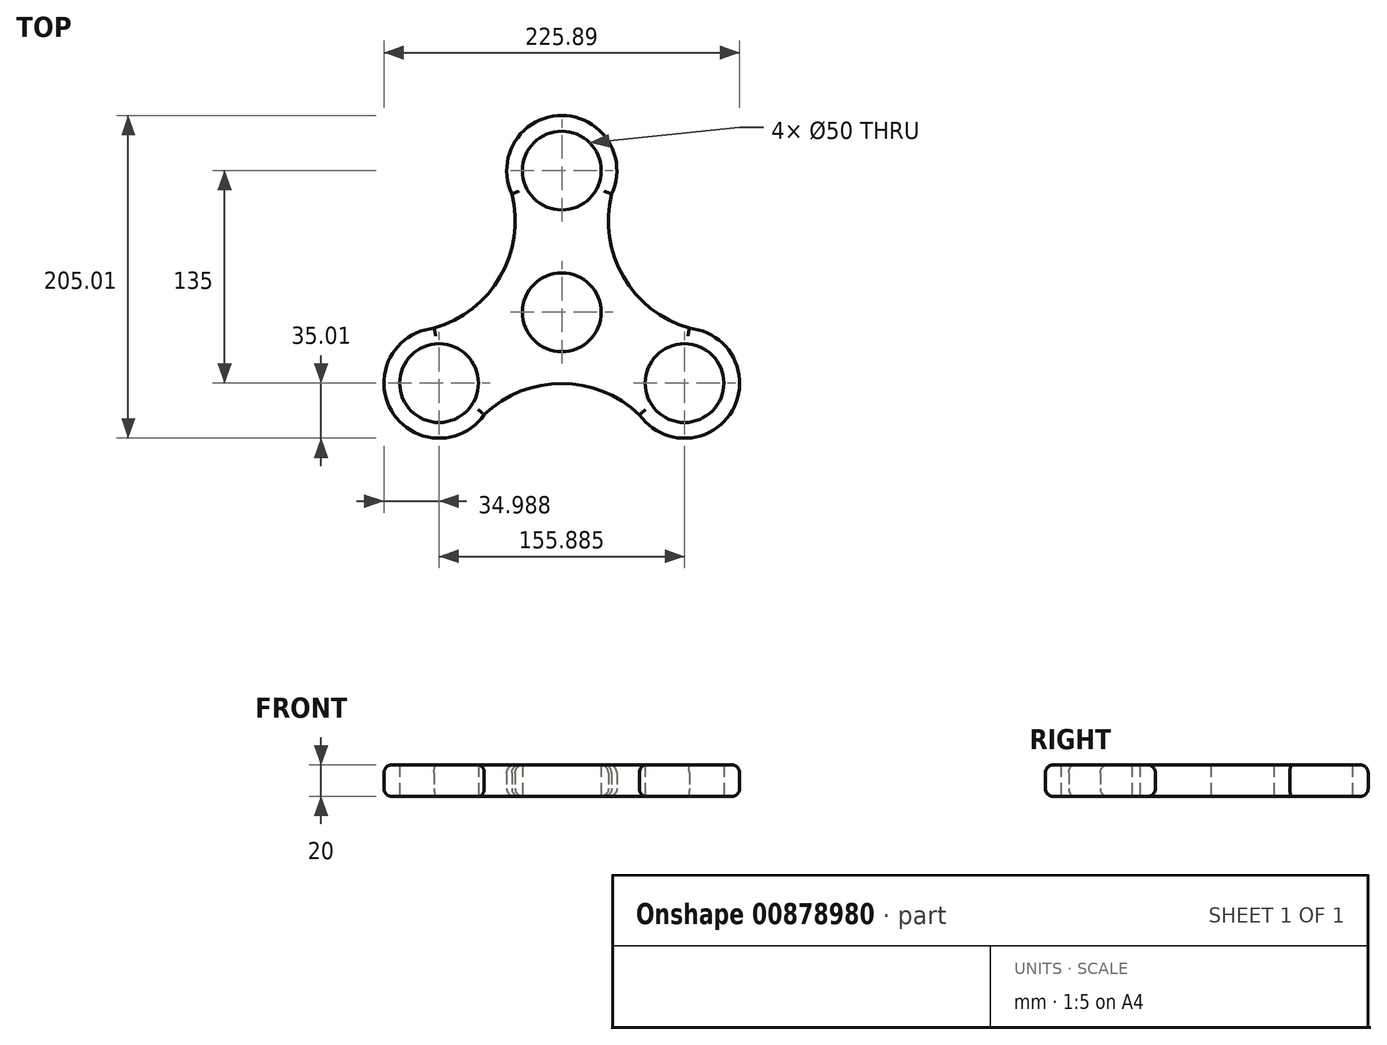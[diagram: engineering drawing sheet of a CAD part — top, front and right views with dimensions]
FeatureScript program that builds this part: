
annotation { "Feature Type Name" : "Feature", "Feature Type Description" : "" }
export const myFeature = defineFeature(function(context is Context, id is Id, definition is map)
    precondition{}
    {
        {
            var Q0;
            Q0=qCreatedBy(makeId("Top.planeOp"),FACE);
            var sketch = newSketch(context, id + "F0", { "sketchPlane" : qUnion([Q0])});
            skCircle(sketch, "E0", {"center": v(0, 0) * mm, "radius": 25 * mm});
            skCircle(sketch, "E1", {"center": v(0, 90) * mm, "radius": 25 * mm});
            skCircle(sketch, "E2.1.0", {"center": v(77.94, -45) * mm, "radius": 25 * mm});
            skCircle(sketch, "E2.2.0", {"center": v(-77.94, -45) * mm, "radius": 25 * mm});
            skLineSegment(sketch, "E2.anchor1", {"start": v(0, 0) * mm, "end": v(0, 90) * mm, "construction": true});
            skLineSegment(sketch, "E2.anchor2", {"start": v(0, 0) * mm, "end": v(-77.94, -45) * mm, "construction": true});
            skCircle(sketch, "E3", {"center": v(0, 90) * mm, "radius": 35 * mm});
            skCircle(sketch, "E4.1.0", {"center": v(-77.93, -45.01) * mm, "radius": 35 * mm});
            skCircle(sketch, "E4.2.0", {"center": v(77.96, -45) * mm, "radius": 35 * mm});
            skLineSegment(sketch, "E5", {"start": v(0, 90) * mm, "end": v(77.94, -45) * mm, "construction": true});
            skLineSegment(sketch, "E6", {"start": v(34.46, 83.85) * mm, "end": v(89.84, -12.07) * mm, "construction": true});
            skArc(sketch, "E7", {"start": v(34.46, 83.85) * mm, "mid": v(39.14, 22.6) * mm, "end": v(89.84, -12.07) * mm});
            skArc(sketch, "E8.1.0", {"start": v(-89.85, -12.09) * mm, "mid": v(-39.15, 22.6) * mm, "end": v(-34.46, 83.84) * mm});
            skArc(sketch, "E8.2.0", {"start": v(55.39, -71.77) * mm, "mid": v(0, -45.2) * mm, "end": v(-55.37, -71.77) * mm});
            skLineSegment(sketch, "E9.anchor1", {"start": v(0, 0) * mm, "end": v(0, 41.01) * mm, "construction": true});
            skLineSegment(sketch, "E9.anchor2", {"start": v(0, 0) * mm, "end": v(-31.42, 26.36) * mm, "construction": true});
            skPoint(sketch, "E10.0.midPoint", {"position": v(13.3, 35.84) * mm});
            skSolve(sketch);
        }
        {
            var Q0;
            Q0 = qSketchRegion(id + "F0", true);
            extrude(context, id + "F1", {"entities" : qUnion([Q0]), "depth" : 20 * mm, "offsetDistance" : 25 * mm});
        }
        {
            var Q0;
            Q0=makeQuery(id+"F1.opExtrude","CAP_EDGE",EDGE,{"disambiguationData":[OSD([sQuery(id+"F0.wireOp",EDGE,"E4.1.0")])],"isStart":false});
            var Q1;
            Q1=makeQuery(id+"F1.opExtrude","CAP_EDGE",EDGE,{"disambiguationData":[OSD([sQuery(id+"F0.wireOp",EDGE,"E4.2.0")])],"isStart":false});
            var Q2;
            Q2=makeQuery(id+"F1.opExtrude","CAP_EDGE",EDGE,{"disambiguationData":[OSD([sQuery(id+"F0.wireOp",EDGE,"E3")])],"isStart":false});
            var Q3;
            Q3=makeQuery(id+"F1.opExtrude","CAP_EDGE",EDGE,{"disambiguationData":[OSD([sQuery(id+"F0.wireOp",EDGE,"E7")])],"isStart":false});
            var Q4;
            Q4=makeQuery(id+"F1.opExtrude","CAP_EDGE",EDGE,{"disambiguationData":[OSD([sQuery(id+"F0.wireOp",EDGE,"E8.2.0")])],"isStart":true});
            var Q5;
            Q5=makeQuery(id+"F1.opExtrude","CAP_EDGE",EDGE,{"disambiguationData":[OSD([sQuery(id+"F0.wireOp",EDGE,"E4.1.0")])],"isStart":true});
            var Q6;
            Q6=makeQuery(id+"F1.opExtrude","CAP_EDGE",EDGE,{"disambiguationData":[OSD([sQuery(id+"F0.wireOp",EDGE,"E8.1.0")])],"isStart":true});
            var Q7;
            Q7=makeQuery(id+"F1.opExtrude","CAP_EDGE",EDGE,{"disambiguationData":[OSD([sQuery(id+"F0.wireOp",EDGE,"E8.2.0")])],"isStart":false});
            var Q8;
            Q8=makeQuery(id+"F1.opExtrude","CAP_EDGE",EDGE,{"disambiguationData":[OSD([sQuery(id+"F0.wireOp",EDGE,"E8.1.0")])],"isStart":false});
            var Q9;
            Q9=makeQuery(id+"F1.opExtrude","CAP_EDGE",EDGE,{"disambiguationData":[OSD([sQuery(id+"F0.wireOp",EDGE,"E4.2.0")])],"isStart":true});
            var Q10;
            Q10=makeQuery(id+"F1.opExtrude","CAP_EDGE",EDGE,{"disambiguationData":[OSD([sQuery(id+"F0.wireOp",EDGE,"E7")])],"isStart":true});
            var Q11;
            Q11=makeQuery(id+"F1.opExtrude","CAP_EDGE",EDGE,{"disambiguationData":[OSD([sQuery(id+"F0.wireOp",EDGE,"E3")])],"isStart":true});
            fillet(context, id + "F2", {"entities" : qUnion([Q0, Q1, Q2, Q3, Q4, Q5, Q6, Q7, Q8, Q9, Q10, Q11]), "radius" : 5 * mm, "tangentPropagation" : true, "allowEdgeOverflow" : false});
        }
    });
